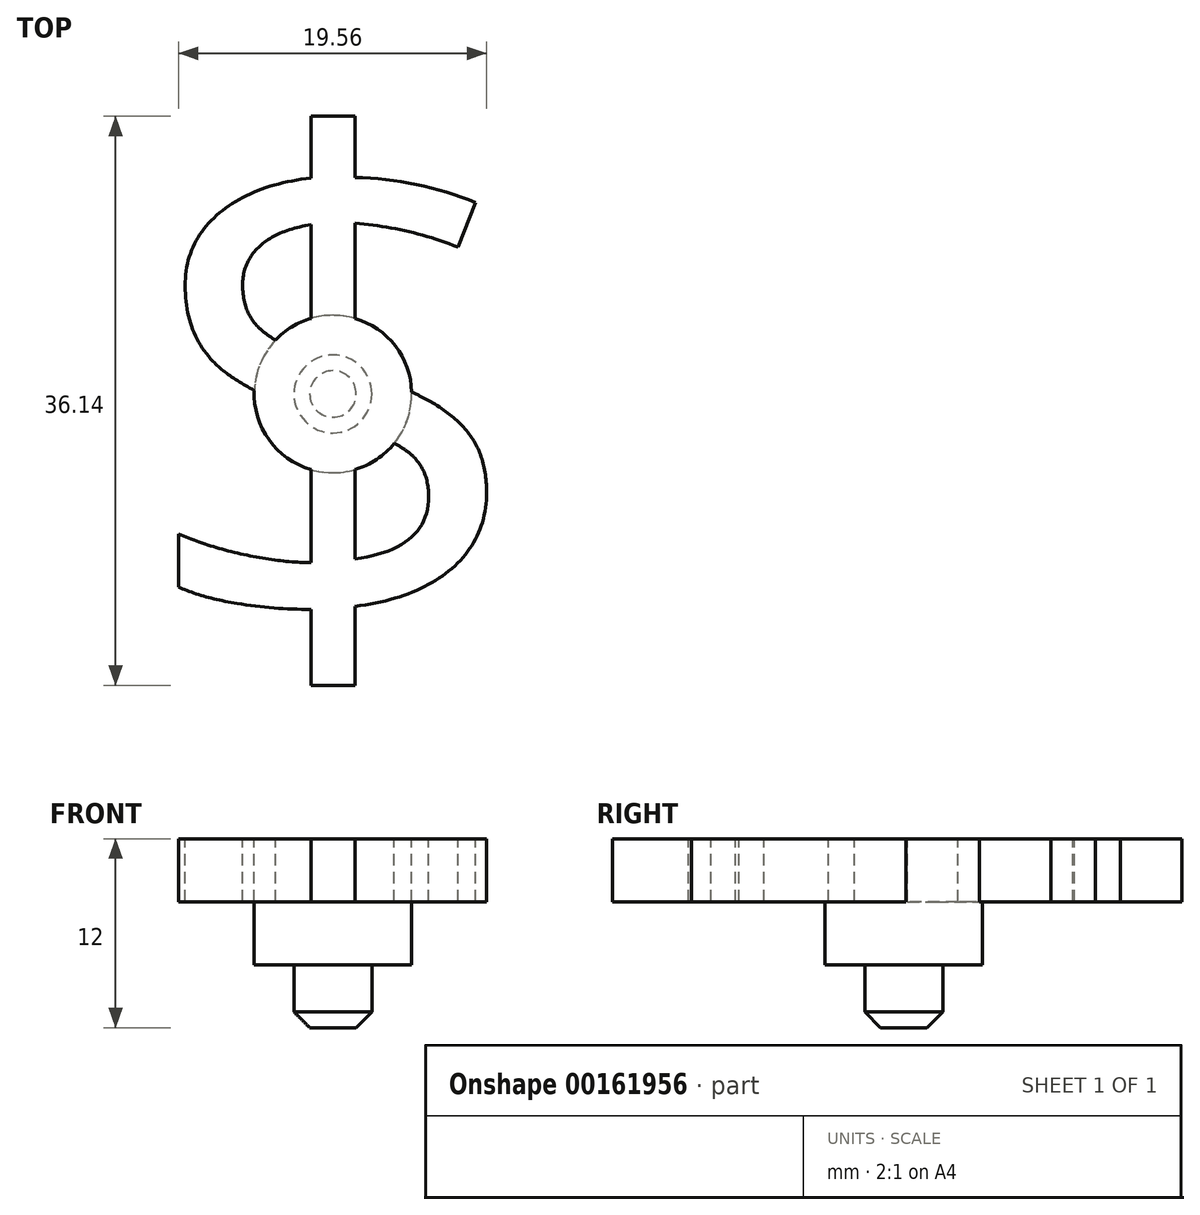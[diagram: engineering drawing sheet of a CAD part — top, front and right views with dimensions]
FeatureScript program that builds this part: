
annotation { "Feature Type Name" : "Feature", "Feature Type Description" : "" }
export const myFeature = defineFeature(function(context is Context, id is Id, definition is map)
    precondition{}
    {
        {
            var Q0;
            Q0=qCreatedBy(makeId("Top.planeOp"),FACE);
            var sketch = newSketch(context, id + "F0", { "sketchPlane" : qUnion([Q0])});
            skText(sketch, "E0", { "text": "$", "fontName": "OpenSans-Regular.ttf"});
            const initialGuessF0  = {"E0": [-0.01263, -0.01593, 1, 0, 0.03186]};
            skSetInitialGuess(sketch, initialGuessF0);
            skSolve(sketch);
        }
        {
            var Q0;
            Q0 = qSketchRegion(id + "F0", true);
            extrude(context, id + "F1", {"entities" : qUnion([Q0]), "oppositeDirection" : true, "depth" : 4 * mm});
        }
        {
            var Q0;
            Q0=makeQuery(id+"F1.opExtrude","CAP_FACE",FACE,{"disambiguationData":[OSD([sQuery(id+"F0.wireOp",EDGE,"E0.sketch_text.stroke-0"),sQuery(id+"F0.wireOp",EDGE,"E0.sketch_text.stroke-1"),sQuery(id+"F0.wireOp",EDGE,"E0.sketch_text.stroke-2"),sQuery(id+"F0.wireOp",EDGE,"E0.sketch_text.stroke-3"),sQuery(id+"F0.wireOp",EDGE,"E0.sketch_text.stroke-4"),sQuery(id+"F0.wireOp",EDGE,"E0.sketch_text.stroke-5"),sQuery(id+"F0.wireOp",EDGE,"E0.sketch_text.stroke-6"),sQuery(id+"F0.wireOp",EDGE,"E0.sketch_text.stroke-7"),sQuery(id+"F0.wireOp",EDGE,"E0.sketch_text.stroke-8"),sQuery(id+"F0.wireOp",EDGE,"E0.sketch_text.stroke-9"),sQuery(id+"F0.wireOp",EDGE,"E0.sketch_text.stroke-10"),sQuery(id+"F0.wireOp",EDGE,"E0.sketch_text.stroke-11"),sQuery(id+"F0.wireOp",EDGE,"E0.sketch_text.stroke-12"),sQuery(id+"F0.wireOp",EDGE,"E0.sketch_text.stroke-13"),sQuery(id+"F0.wireOp",EDGE,"E0.sketch_text.stroke-14"),sQuery(id+"F0.wireOp",EDGE,"E0.sketch_text.stroke-15"),sQuery(id+"F0.wireOp",EDGE,"E0.sketch_text.stroke-16"),sQuery(id+"F0.wireOp",EDGE,"E0.sketch_text.stroke-17"),sQuery(id+"F0.wireOp",EDGE,"E0.sketch_text.stroke-18"),sQuery(id+"F0.wireOp",EDGE,"E0.sketch_text.stroke-19"),sQuery(id+"F0.wireOp",EDGE,"E0.sketch_text.stroke-20"),sQuery(id+"F0.wireOp",EDGE,"E0.sketch_text.stroke-21"),sQuery(id+"F0.wireOp",EDGE,"E0.sketch_text.stroke-22"),sQuery(id+"F0.wireOp",EDGE,"E0.sketch_text.stroke-23"),sQuery(id+"F0.wireOp",EDGE,"E0.sketch_text.stroke-24"),sQuery(id+"F0.wireOp",EDGE,"E0.sketch_text.stroke-25"),sQuery(id+"F0.wireOp",EDGE,"E0.sketch_text.stroke-26"),sQuery(id+"F0.wireOp",EDGE,"E0.sketch_text.stroke-27"),sQuery(id+"F0.wireOp",EDGE,"E0.sketch_text.stroke-28"),sQuery(id+"F0.wireOp",EDGE,"E0.sketch_text.stroke-29"),sQuery(id+"F0.wireOp",EDGE,"E0.sketch_text.stroke-30"),sQuery(id+"F0.wireOp",EDGE,"E0.sketch_text.stroke-31"),sQuery(id+"F0.wireOp",EDGE,"E0.sketch_text.stroke-32"),sQuery(id+"F0.wireOp",EDGE,"E0.sketch_text.stroke-33")])],"isStart":false});
            var sketch = newSketch(context, id + "F2", { "sketchPlane" : qUnion([Q0])});
            skCircle(sketch, "E1", {"center": v(0, 0) * mm, "radius": 5 * mm});
            skSolve(sketch);
        }
        {
            var Q0;
            Q0 = qSketchRegion(id + "F2", true);
            extrude(context, id + "F3", {"entities" : qUnion([Q0]), "operationType" : NewBodyOperationType.ADD, "depth" : 8 * mm, "symmetric" : true});
        }
        {
            var Q0;
            Q0=makeQuery(id+"F3.opExtrude","CAP_FACE",FACE,{"disambiguationData":[OSD([sQuery(id+"F2.wireOp",EDGE,"E1")])],"isStart":false});
            var sketch = newSketch(context, id + "F4", { "sketchPlane" : qUnion([Q0])});
            skCircle(sketch, "E2", {"center": v(0, 0) * mm, "radius": 2.48 * mm});
            skSolve(sketch);
        }
        {
            var Q0;
            Q0 = qSketchRegion(id + "F4", true);
            extrude(context, id + "F5", {"entities" : qUnion([Q0]), "operationType" : NewBodyOperationType.ADD, "depth" : 4 * mm});
        }
        {
            var Q0;
            Q0=makeQuery(id+"F5.opExtrude","CAP_EDGE",EDGE,{"disambiguationData":[OSD([sQuery(id+"F4.wireOp",EDGE,"E2")])],"isStart":false});
            chamfer(context, id + "F6", {"entities" : qUnion([Q0]), "width" : 1 * mm, "tangentPropagation" : true});
        }
    });
